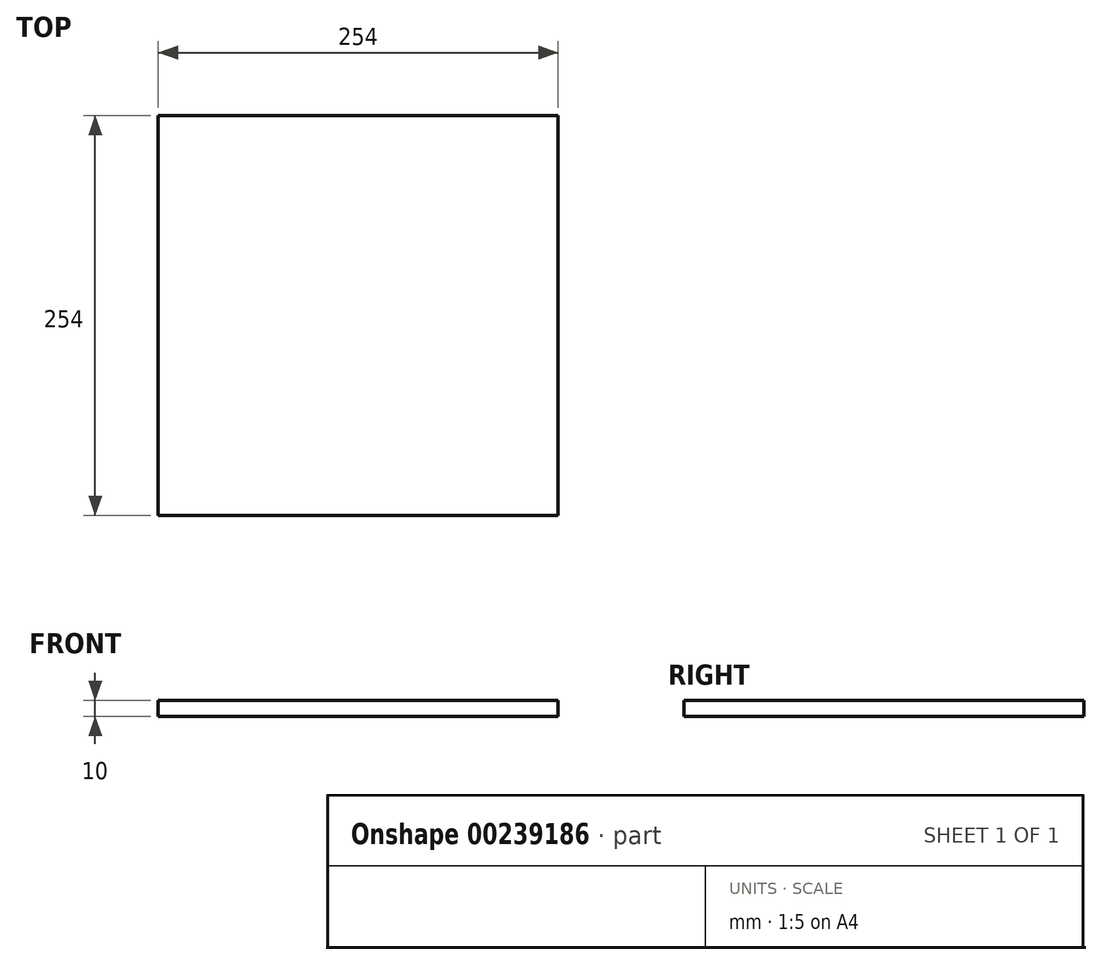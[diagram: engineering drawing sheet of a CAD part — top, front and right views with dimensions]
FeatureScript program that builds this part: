
annotation { "Feature Type Name" : "Feature", "Feature Type Description" : "" }
export const myFeature = defineFeature(function(context is Context, id is Id, definition is map)
    precondition{}
    {
        {
            assignVariable(context, id + "F0", {"name" : "l", "anyValue" : 10});
        }
        {
            var Q0;
            Q0=qCreatedBy(makeId("Top.planeOp"),FACE);
            var sketch = newSketch(context, id + "F1", { "sketchPlane" : qUnion([Q0])});
            skLineSegment(sketch, "E0.bottom", {"start": v(127, 127) * mm, "end": v(-127, 127) * mm});
            skLineSegment(sketch, "E0.top", {"start": v(127, -127) * mm, "end": v(-127, -127) * mm});
            skLineSegment(sketch, "E0.left", {"start": v(127, 127) * mm, "end": v(127, -127) * mm});
            skLineSegment(sketch, "E0.right", {"start": v(-127, 127) * mm, "end": v(-127, -127) * mm});
            skPoint(sketch, "E0.middle", {"position": v(0, 0) * mm});
            skSolve(sketch);
        }
        {
            var Q0;
            Q0=makeQuery(id+"F1.imprint","IMPRINT",FACE,{"disambiguationData":[TD([[makeQuery(id+"F1.imprint","IMPRINT",EDGE,{"derivedFrom":sQuery(id+"F1.wireOp",EDGE,"E0.bottom")}),1.0]])]});
            extrude(context, id + "F2", {"entities" : qUnion([Q0]), "endBound" : BoundingType.SYMMETRIC, "depth" : (getVariable(context, 'l')) * mm});
        }
    });
